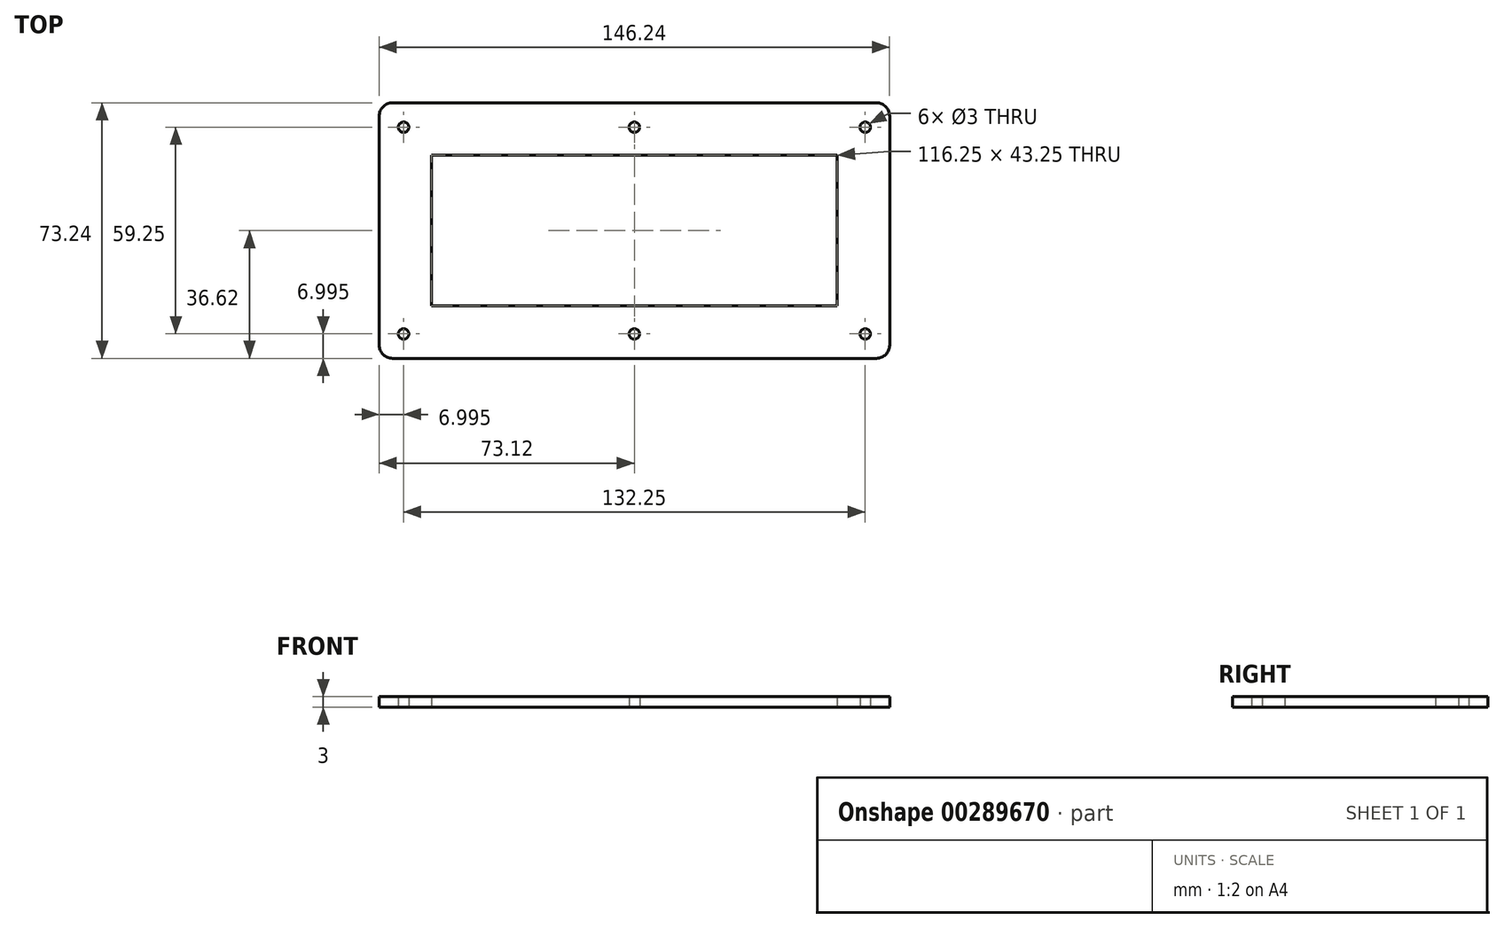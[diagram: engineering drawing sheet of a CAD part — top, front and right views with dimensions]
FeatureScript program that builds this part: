
annotation { "Feature Type Name" : "Feature", "Feature Type Description" : "" }
export const myFeature = defineFeature(function(context is Context, id is Id, definition is map)
    precondition{}
    {
        {
            var Q0;
            Q0=qCreatedBy(makeId("Top.planeOp"),FACE);
            var sketch = newSketch(context, id + "F0", { "sketchPlane" : qUnion([Q0])});
            skLineSegment(sketch, "E0.bottom", {"start": v(-69.31, 36.62) * mm, "end": v(69.32, 36.62) * mm});
            skLineSegment(sketch, "E0.top", {"start": v(-69.31, -36.62) * mm, "end": v(69.31, -36.62) * mm});
            skLineSegment(sketch, "E0.left", {"start": v(-73.12, 32.82) * mm, "end": v(-73.12, -32.81) * mm});
            skLineSegment(sketch, "E0.right", {"start": v(73.12, 32.82) * mm, "end": v(73.12, -32.81) * mm});
            skPoint(sketch, "E0.middle", {"position": v(0, 0) * mm});
            skPoint(sketch, "E1.visualSharp", {"position": v(-73.12, 36.62) * mm});
            skArc(sketch, "E1.filletArc", {"start": v(-69.31, 36.63) * mm, "mid": v(-72, 35.5) * mm, "end": v(-73.12, 32.82) * mm});
            skPoint(sketch, "E2.visualSharp", {"position": v(-73.12, -36.62) * mm});
            skArc(sketch, "E2.filletArc", {"start": v(-73.12, -32.81) * mm, "mid": v(-72, -35.5) * mm, "end": v(-69.31, -36.62) * mm});
            skPoint(sketch, "E3.visualSharp", {"position": v(73.12, -36.62) * mm});
            skArc(sketch, "E3.filletArc", {"start": v(69.31, -36.62) * mm, "mid": v(72, -35.5) * mm, "end": v(73.12, -32.81) * mm});
            skPoint(sketch, "E4.visualSharp", {"position": v(73.12, 36.62) * mm});
            skArc(sketch, "E4.filletArc", {"start": v(73.12, 32.82) * mm, "mid": v(72, 35.5) * mm, "end": v(69.32, 36.62) * mm});
            skLineSegment(sketch, "E5.bottom", {"start": v(-58.12, 21.62) * mm, "end": v(58.12, 21.62) * mm});
            skLineSegment(sketch, "E5.top", {"start": v(-58.12, -21.62) * mm, "end": v(58.12, -21.62) * mm});
            skLineSegment(sketch, "E5.left", {"start": v(-58.12, 21.62) * mm, "end": v(-58.12, -21.62) * mm});
            skLineSegment(sketch, "E5.right", {"start": v(58.12, 21.62) * mm, "end": v(58.12, -21.62) * mm});
            skLineSegment(sketch, "E6.bottom", {"start": v(-66.12, 29.62) * mm, "end": v(66.12, 29.62) * mm});
            skLineSegment(sketch, "E6.top", {"start": v(-66.12, -29.62) * mm, "end": v(66.12, -29.62) * mm});
            skLineSegment(sketch, "E6.left", {"start": v(-66.12, 29.62) * mm, "end": v(-66.12, -29.62) * mm});
            skLineSegment(sketch, "E6.right", {"start": v(66.12, 29.62) * mm, "end": v(66.12, -29.62) * mm});
            skCircle(sketch, "E7", {"center": v(-66.12, 29.62) * mm, "radius": 1.5 * mm});
            skCircle(sketch, "E8", {"center": v(0, 29.62) * mm, "radius": 1.5 * mm});
            skCircle(sketch, "E9", {"center": v(66.12, 29.62) * mm, "radius": 1.5 * mm});
            skCircle(sketch, "E10", {"center": v(-66.12, -29.62) * mm, "radius": 1.5 * mm});
            skCircle(sketch, "E11", {"center": v(0, -29.62) * mm, "radius": 1.5 * mm});
            skCircle(sketch, "E12", {"center": v(66.12, -29.62) * mm, "radius": 1.5 * mm});
            skSolve(sketch);
        }
        {
            var Q0;
            Q0 = qSketchRegion(id + "F0", true);
            var Q1;
            Q1=makeQuery(id+"F0.imprint","IMPRINT",FACE,{"disambiguationData":[TD([[makeQuery(id+"F0.imprint","IMPRINT",EDGE,{"derivedFrom":sQuery(id+"F0.wireOp",EDGE,"E5.bottom")}),1.0]])]});
            extrude(context, id + "F1", {"entities" : qUnion([Q0, Q1]), "depth" : 3 * mm});
        }
    });
